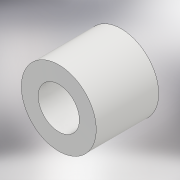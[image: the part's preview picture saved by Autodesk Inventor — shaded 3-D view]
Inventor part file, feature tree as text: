
AUTODESK INVENTOR PART (.ipt)
format: ipt  version: 2018.2 (Build 222227000, 227)  size: 105,984 bytes
history: native  units: mm
features: extrude x1, sketch x1
ambient origin geometry x8: Origin, YZ Plane, XZ Plane, XY Plane, X Axis, Y Axis, Z Axis, Center Point
bodies: Solid1 (feature_tree)
feature tree (2):
  extrude  "Extrusion1"  Depth=5.0mm
  sketch  "Sketch1"  dims[d0=6.0mm d1=3.3mm d2=5.0mm d3=0.0mm]
